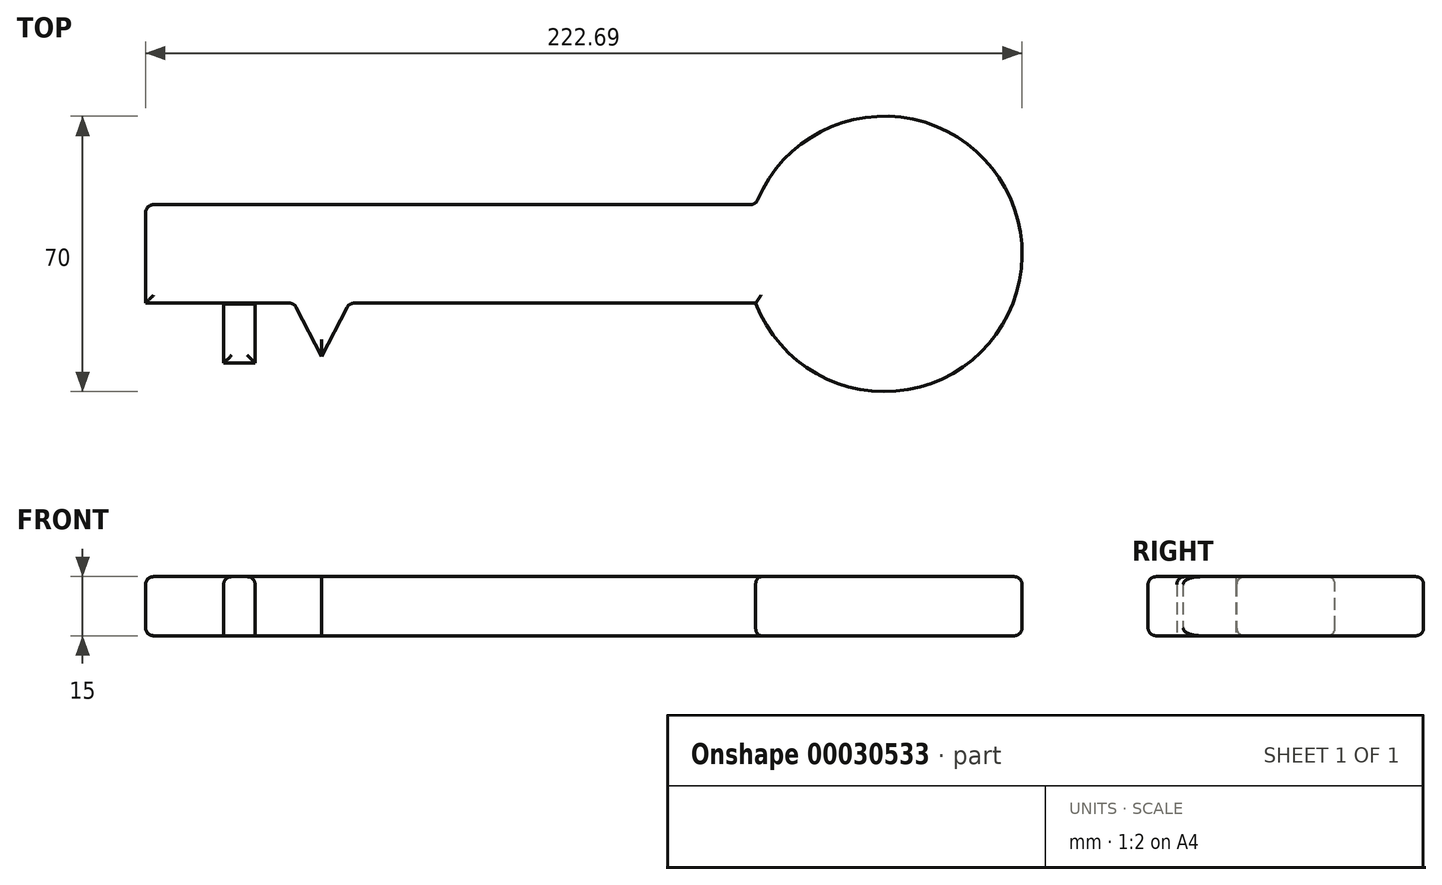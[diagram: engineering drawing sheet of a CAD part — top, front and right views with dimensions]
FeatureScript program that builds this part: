
annotation { "Feature Type Name" : "Feature", "Feature Type Description" : "" }
export const myFeature = defineFeature(function(context is Context, id is Id, definition is map)
    precondition{}
    {
        {
            var Q0;
            Q0=qCreatedBy(makeId("Top.planeOp"),FACE);
            var sketch = newSketch(context, id + "F0", { "sketchPlane" : qUnion([Q0])});
            skLineSegment(sketch, "E0.bottom", {"start": v(21.45, 38.6) * mm, "end": v(-133.55, 38.6) * mm});
            skLineSegment(sketch, "E0.top", {"start": v(21.45, 13.6) * mm, "end": v(-133.55, 13.6) * mm});
            skLineSegment(sketch, "E0.right", {"start": v(-133.55, 38.6) * mm, "end": v(-133.55, 13.6) * mm});
            skLineSegment(sketch, "E1.bottom", {"start": v(-133.55, 13.6) * mm, "end": v(-123.55, 13.6) * mm});
            skLineSegment(sketch, "E1.top", {"start": v(-133.55, -16.4) * mm, "end": v(-123.55, -16.4) * mm});
            skLineSegment(sketch, "E1.left", {"start": v(-133.55, 13.6) * mm, "end": v(-133.55, -16.4) * mm});
            skLineSegment(sketch, "E1.right", {"start": v(-123.55, 13.6) * mm, "end": v(-123.55, -16.4) * mm});
            skLineSegment(sketch, "E2.bottom", {"start": v(-113.71, 13.37) * mm, "end": v(-105.71, 13.37) * mm});
            skLineSegment(sketch, "E2.top", {"start": v(-113.71, -1.63) * mm, "end": v(-105.71, -1.63) * mm});
            skLineSegment(sketch, "E2.left", {"start": v(-113.71, 13.37) * mm, "end": v(-113.71, -1.63) * mm});
            skLineSegment(sketch, "E2.right", {"start": v(-105.71, 13.37) * mm, "end": v(-105.71, -1.63) * mm});
            skLineSegment(sketch, "E3", {"start": v(-95.82, 13.6) * mm, "end": v(-88.82, 0) * mm});
            skLineSegment(sketch, "E4", {"start": v(-88.82, 0) * mm, "end": v(-81.82, 13.6) * mm});
            skCircle(sketch, "E5", {"center": v(54.14, 26.1) * mm, "radius": 17.5 * mm});
            skArc(sketch, "E6", {"start": v(21.45, 13.6) * mm, "mid": v(89.14, 26.1) * mm, "end": v(21.45, 38.6) * mm});
            skLineSegment(sketch, "E7", {"start": v(-133.55, 26.1) * mm, "end": v(54.14, 26.1) * mm, "construction": true});
            skSolve(sketch);
        }
        {
            var Q0;
            Q0=makeQuery(id+"F0.imprint","IMPRINT",FACE,{"disambiguationData":[TD([[makeQuery(id+"F0.imprint","IMPRINT",EDGE,{"derivedFrom":sQuery(id+"F0.wireOp",EDGE,"E0.bottom")}),1.0]])]});
            var Q1;
            Q1=makeQuery(id+"F0.imprint","IMPRINT",FACE,{"disambiguationData":[TD([[makeQuery(id+"F0.imprint","IMPRINT",EDGE,{"derivedFrom":sQuery(id+"F0.wireOp",EDGE,"E1.bottom")}),-1.0]])]});
            var Q2;
            {var subQ1=sQuery(id+"F0.wireOp",EDGE,"E3");Q2=makeQuery(id+"F0.imprint","IMPRINT",FACE,{"disambiguationData":[TD([[makeQuery(id+"F0.imprint","IMPRINT",EDGE,{"derivedFrom":subQ1}),1.0]])]});}
            var Q3;
            Q3=makeQuery(id+"F0.imprint","IMPRINT",FACE,{"disambiguationData":[TD([[makeQuery(id+"F0.imprint","IMPRINT",EDGE,{"derivedFrom":sQuery(id+"F0.wireOp",EDGE,"E5")}),1.0]])]});
            var Q4;
            Q4=makeQuery(id+"F0.imprint","IMPRINT",FACE,{"disambiguationData":[TD([[makeQuery(id+"F0.imprint","IMPRINT",EDGE,{"derivedFrom":sQuery(id+"F0.wireOp",EDGE,"E2.bottom")}),-1.0]])]});
            extrude(context, id + "F1", {"entities" : qUnion([Q0, Q1, Q2, Q3, Q4]), "depth" : 15 * mm});
        }
        {
            var Q0;
            Q0=makeQuery(id+"F1.opExtrude","CAP_EDGE",EDGE,{"disambiguationData":[OSD([sQuery(id+"F0.wireOp",EDGE,"E0.bottom")])],"isStart":false});
            var Q1;
            Q1=makeQuery(id+"F1.opExtrude","CAP_EDGE",EDGE,{"disambiguationData":[OSD([sQuery(id+"F0.wireOp",EDGE,"E0.right"),sQuery(id+"F0.wireOp",EDGE,"E1.left")])],"isStart":false});
            var Q2;
            Q2=makeQuery(id+"F1.opExtrude","CAP_EDGE",EDGE,{"disambiguationData":[OSD([sQuery(id+"F0.wireOp",EDGE,"E1.right")])],"isStart":false});
            var Q3;
            {var subQ0=sQuery(id+"F0.wireOp",EDGE,"E0.top");Q3=makeQuery(id+"F1.opExtrude","CAP_EDGE",EDGE,{"disambiguationData":[OSD([subQ0]),TDD([makeQuery(id+"F0.imprint","IMPRINT",EDGE,{"disambiguationData":[TD([[makeQuery(id+"F0.imprint","INTERSECT",VERTEX,{"derivedFrom":[subQ0,sQuery(id+"F0.wireOp",EDGE,"E3")]}),-1.0]])],"derivedFrom":subQ0})])],"isStart":false});}
            var Q4;
            Q4=makeQuery(id+"F1.opExtrude","CAP_EDGE",EDGE,{"disambiguationData":[OSD([sQuery(id+"F0.wireOp",EDGE,"E2.left")])],"isStart":false});
            var Q5;
            Q5=makeQuery(id+"F1.opExtrude","CAP_EDGE",EDGE,{"disambiguationData":[OSD([sQuery(id+"F0.wireOp",EDGE,"E2.top")])],"isStart":false});
            var Q6;
            Q6=makeQuery(id+"F1.opExtrude","CAP_EDGE",EDGE,{"disambiguationData":[OSD([sQuery(id+"F0.wireOp",EDGE,"E2.right")])],"isStart":false});
            var Q7;
            Q7=makeQuery(id+"F1.opExtrude","CAP_EDGE",EDGE,{"disambiguationData":[OSD([sQuery(id+"F0.wireOp",EDGE,"E3")])],"isStart":false});
            var Q8;
            Q8=makeQuery(id+"F1.opExtrude","CAP_EDGE",EDGE,{"disambiguationData":[OSD([sQuery(id+"F0.wireOp",EDGE,"E4")])],"isStart":false});
            var Q9;
            {var subQ0=sQuery(id+"F0.wireOp",EDGE,"E0.top");Q9=makeQuery(id+"F1.opExtrude","CAP_EDGE",EDGE,{"disambiguationData":[OSD([subQ0]),TDD([makeQuery(id+"F0.imprint","IMPRINT",EDGE,{"disambiguationData":[TD([[makeQuery(id+"F0.imprint","INTERSECT",VERTEX,{"derivedFrom":[subQ0,sQuery(id+"F0.wireOp",EDGE,"E6")]}),-1.0]])],"derivedFrom":subQ0})])],"isStart":false});}
            var Q10;
            Q10=makeQuery(id+"F1.opExtrude","CAP_EDGE",EDGE,{"disambiguationData":[OSD([sQuery(id+"F0.wireOp",EDGE,"E6")])],"isStart":false});
            var Q11;
            Q11=makeQuery(id+"F1.opExtrude","SWEPT_FACE",FACE,{"disambiguationData":[OSD([sQuery(id+"F0.wireOp",EDGE,"E0.bottom")])]});
            var Q12;
            Q12=makeQuery(id+"F1.opExtrude","CAP_EDGE",EDGE,{"disambiguationData":[OSD([sQuery(id+"F0.wireOp",EDGE,"E6")])],"isStart":true});
            var Q13;
            {var subQ0=sQuery(id+"F0.wireOp",EDGE,"E0.top");Q13=makeQuery(id+"F1.opExtrude","CAP_EDGE",EDGE,{"disambiguationData":[OSD([subQ0]),TDD([makeQuery(id+"F0.imprint","IMPRINT",EDGE,{"disambiguationData":[TD([[makeQuery(id+"F0.imprint","INTERSECT",VERTEX,{"derivedFrom":[subQ0,sQuery(id+"F0.wireOp",EDGE,"E3")]}),-1.0]])],"derivedFrom":subQ0})])],"isStart":true});}
            var Q14;
            Q14=makeQuery(id+"F1.opExtrude","CAP_EDGE",EDGE,{"disambiguationData":[OSD([sQuery(id+"F0.wireOp",EDGE,"E1.right")])],"isStart":true});
            var Q15;
            Q15=makeQuery(id+"F1.opExtrude","CAP_EDGE",EDGE,{"disambiguationData":[OSD([sQuery(id+"F0.wireOp",EDGE,"E3")])],"isStart":true});
            var Q16;
            Q16=makeQuery(id+"F1.opExtrude","SWEPT_EDGE",EDGE,{"disambiguationData":[OSD([sQuery(id+"F0.wireOp",EDGE,"E0.top"),sQuery(id+"F0.wireOp",EDGE,"E3")])]});
            var Q17;
            Q17=makeQuery(id+"F1.opExtrude","SWEPT_EDGE",EDGE,{"disambiguationData":[OSD([sQuery(id+"F0.wireOp",EDGE,"E0.top"),sQuery(id+"F0.wireOp",EDGE,"E4")])]});
            var Q18;
            Q18=makeQuery(id+"F1.opExtrude","CAP_EDGE",EDGE,{"disambiguationData":[OSD([sQuery(id+"F0.wireOp",EDGE,"E4")])],"isStart":true});
            var Q19;
            Q19=makeQuery(id+"F1.opExtrude","CAP_EDGE",EDGE,{"disambiguationData":[OSD([sQuery(id+"F0.wireOp",EDGE,"E1.top")])],"isStart":false});
            var Q20;
            Q20=makeQuery(id+"F1.opExtrude","CAP_FACE",FACE,{"disambiguationData":[OSD([sQuery(id+"F0.wireOp",EDGE,"E0.bottom"),sQuery(id+"F0.wireOp",EDGE,"E0.top"),sQuery(id+"F0.wireOp",EDGE,"E0.right"),sQuery(id+"F0.wireOp",EDGE,"E1.top"),sQuery(id+"F0.wireOp",EDGE,"E1.left"),sQuery(id+"F0.wireOp",EDGE,"E1.right"),sQuery(id+"F0.wireOp",EDGE,"E3"),sQuery(id+"F0.wireOp",EDGE,"E4"),sQuery(id+"F0.wireOp",EDGE,"E6")])],"isStart":true});
            fillet(context, id + "F2", {"entities" : qUnion([Q0, Q1, Q2, Q3, Q4, Q5, Q6, Q7, Q8, Q9, Q10, Q11, Q12, Q13, Q14, Q15, Q16, Q17, Q18, Q19, Q20]), "radius" : 2 * mm, "tangentPropagation" : true, "allowEdgeOverflow" : false});
        }
    });
